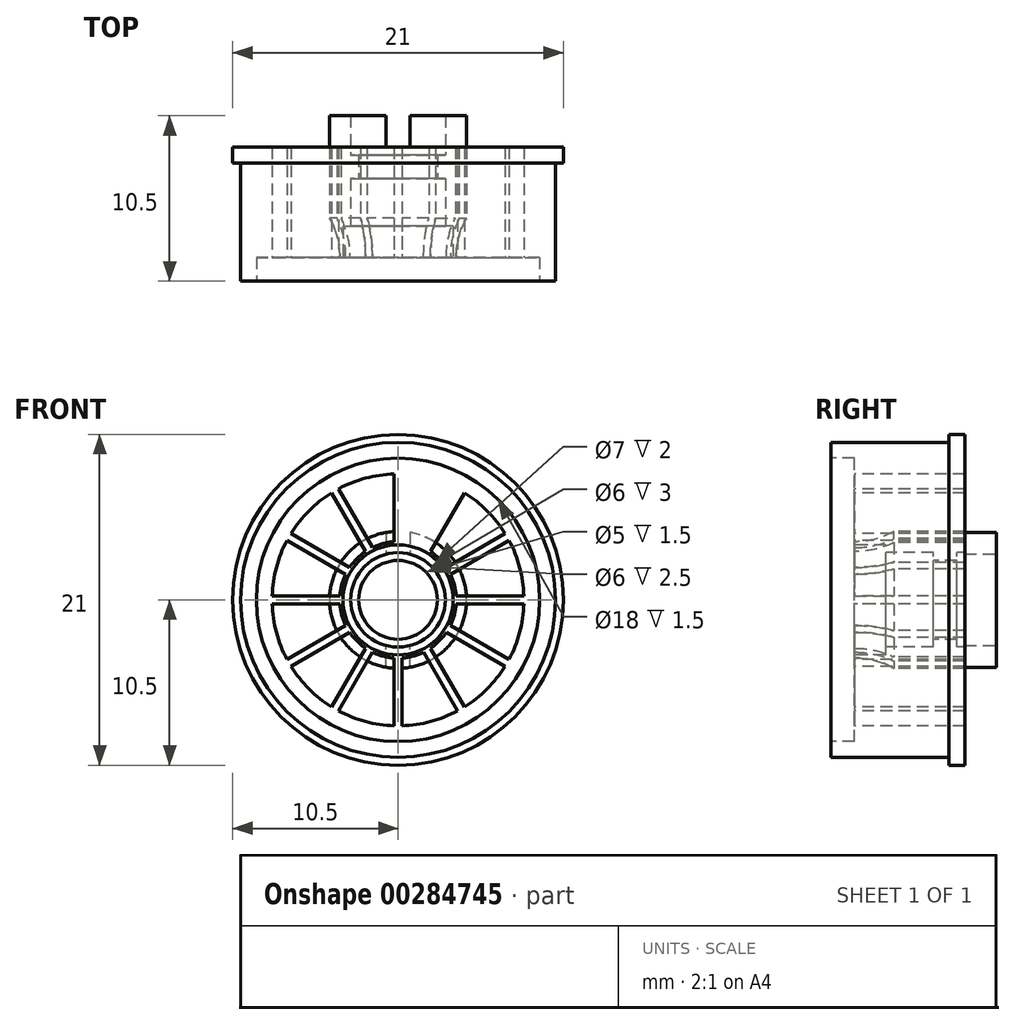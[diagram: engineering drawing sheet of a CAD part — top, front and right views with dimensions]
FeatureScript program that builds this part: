
annotation { "Feature Type Name" : "Feature", "Feature Type Description" : "" }
export const myFeature = defineFeature(function(context is Context, id is Id, definition is map)
    precondition{}
    {
        {
            var Q0;
            Q0=qCreatedBy(makeId("Front.planeOp"),FACE);
            var sketch = newSketch(context, id + "F0", { "sketchPlane" : qUnion([Q0])});
            skCircle(sketch, "E0", {"center": v(0, 0) * mm, "radius": 10.5 * mm});
            skSolve(sketch);
        }
        {
            var Q0;
            Q0=makeQuery(id+"F0.imprint","IMPRINT",FACE,{"disambiguationData":[TD([[makeQuery(id+"F0.imprint","IMPRINT",EDGE,{"derivedFrom":sQuery(id+"F0.wireOp",EDGE,"E0")}),1.0]])]});
            extrude(context, id + "F1", {"entities" : qUnion([Q0]), "depth" : 1 * mm});
        }
        {
            var Q0;
            Q0=makeQuery(id+"F1.opExtrude","CAP_FACE",FACE,{"disambiguationData":[OSD([sQuery(id+"F0.wireOp",EDGE,"E0")])],"isStart":false});
            var sketch = newSketch(context, id + "F2", { "sketchPlane" : qUnion([Q0])});
            skCircle(sketch, "E1", {"center": v(0, 0) * mm, "radius": 10 * mm});
            skSolve(sketch);
        }
        {
            var Q0;
            Q0=makeQuery(id+"F2.imprint","IMPRINT",FACE,{"disambiguationData":[TD([[makeQuery(id+"F2.imprint","IMPRINT",EDGE,{"derivedFrom":sQuery(id+"F2.wireOp",EDGE,"E1")}),1.0]])]});
            extrude(context, id + "F3", {"entities" : qUnion([Q0]), "operationType" : NewBodyOperationType.ADD, "depth" : 7.5 * mm});
        }
        {
            var Q0;
            Q0=makeQuery(id+"F3.opExtrude","CAP_FACE",FACE,{"disambiguationData":[OSD([sQuery(id+"F2.wireOp",EDGE,"E1")])],"isStart":false});
            var sketch = newSketch(context, id + "F4", { "sketchPlane" : qUnion([Q0])});
            skCircle(sketch, "E2", {"center": v(0, 0) * mm, "radius": 3.5 * mm});
            skSolve(sketch);
        }
        {
            var Q0;
            Q0=makeQuery(id+"F4.imprint","IMPRINT",FACE,{"disambiguationData":[TD([[makeQuery(id+"F4.imprint","IMPRINT",EDGE,{"derivedFrom":sQuery(id+"F4.wireOp",EDGE,"E2")}),1.0]])]});
            extrude(context, id + "F5", {"entities" : qUnion([Q0]), "operationType" : NewBodyOperationType.REMOVE, "oppositeDirection" : true, "depth" : 3.5 * mm});
        }
        {
            var Q0;
            Q0=makeQuery(id+"F5.boolean.opBoolean","COPY",FACE,{"derivedFrom":makeQuery(id+"F5.opExtrude","CAP_FACE",FACE,{"disambiguationData":[OSD([sQuery(id+"F4.wireOp",EDGE,"E2")])],"isStart":false})});
            var sketch = newSketch(context, id + "F6", { "sketchPlane" : qUnion([Q0])});
            skCircle(sketch, "E3", {"center": v(0, 0) * mm, "radius": 3 * mm});
            skSolve(sketch);
        }
        {
            var Q0;
            Q0=makeQuery(id+"F6.imprint","IMPRINT",FACE,{"disambiguationData":[TD([[makeQuery(id+"F6.imprint","IMPRINT",EDGE,{"derivedFrom":sQuery(id+"F6.wireOp",EDGE,"E3")}),1.0]])]});
            extrude(context, id + "F7", {"entities" : qUnion([Q0]), "operationType" : NewBodyOperationType.REMOVE, "oppositeDirection" : true, "depth" : 3 * mm});
        }
        {
            var Q0;
            Q0=makeQuery(id+"F7.boolean.opBoolean","COPY",FACE,{"derivedFrom":makeQuery(id+"F7.opExtrude","CAP_FACE",FACE,{"disambiguationData":[OSD([sQuery(id+"F6.wireOp",EDGE,"E3")])],"isStart":false})});
            var sketch = newSketch(context, id + "F8", { "sketchPlane" : qUnion([Q0])});
            skCircle(sketch, "E4", {"center": v(0, 0) * mm, "radius": 2.5 * mm});
            skSolve(sketch);
        }
        {
            var Q0;
            Q0=makeQuery(id+"F8.imprint","IMPRINT",FACE,{"disambiguationData":[TD([[makeQuery(id+"F8.imprint","IMPRINT",EDGE,{"derivedFrom":sQuery(id+"F8.wireOp",EDGE,"E4")}),1.0]])]});
            extrude(context, id + "F9", {"entities" : qUnion([Q0]), "operationType" : NewBodyOperationType.REMOVE, "oppositeDirection" : true, "depth" : 1.5 * mm});
        }
        {
            var Q0;
            Q0=makeQuery(id+"F9.boolean.opBoolean","COPY",FACE,{"derivedFrom":makeQuery(id+"F9.opExtrude","CAP_FACE",FACE,{"disambiguationData":[OSD([sQuery(id+"F8.wireOp",EDGE,"E4")])],"isStart":false})});
            var sketch = newSketch(context, id + "F10", { "sketchPlane" : qUnion([Q0])});
            skCircle(sketch, "E5", {"center": v(0, 0) * mm, "radius": 3 * mm});
            skSolve(sketch);
        }
        {
            var Q0;
            Q0=qSketchRegion(id+"F10",true);
            extrude(context, id + "F11", {"entities" : qUnion([Q0]), "operationType" : NewBodyOperationType.REMOVE, "oppositeDirection" : true, "depth" : 25 * mm});
        }
        {
            var Q0;
            Q0=makeQuery(id+"F3.opExtrude","CAP_FACE",FACE,{"disambiguationData":[OSD([sQuery(id+"F2.wireOp",EDGE,"E1")])],"isStart":false});
            var sketch = newSketch(context, id + "F12", { "sketchPlane" : qUnion([Q0])});
            skCircle(sketch, "E6", {"center": v(0, 0) * mm, "radius": 9 * mm});
            skSolve(sketch);
        }
        {
            var Q0;
            Q0=makeQuery(id+"F1.opExtrude","CAP_FACE",FACE,{"disambiguationData":[OSD([sQuery(id+"F0.wireOp",EDGE,"E0")])],"isStart":true});
            var sketch = newSketch(context, id + "F13", { "sketchPlane" : qUnion([Q0])});
            skCircle(sketch, "E7", {"center": v(0, 0) * mm, "radius": 9 * mm});
            skCircle(sketch, "E8", {"center": v(0, 0) * mm, "radius": 4.35 * mm});
            skSolve(sketch);
        }
        {
            var Q0;
            Q0=makeQuery(id+"F13.imprint","IMPRINT",FACE,{"disambiguationData":[TD([[makeQuery(id+"F13.imprint","IMPRINT",EDGE,{"derivedFrom":sQuery(id+"F13.wireOp",EDGE,"E7")}),1.0]])]});
            extrude(context, id + "F14", {"entities" : qUnion([Q0]), "operationType" : NewBodyOperationType.REMOVE, "oppositeDirection" : true, "depth" : 4.5 * mm});
        }
        {
            var Q0;
            Q0=makeQuery(id+"F12.imprint","IMPRINT",FACE,{"disambiguationData":[TD([[makeQuery(id+"F12.imprint","IMPRINT",EDGE,{"derivedFrom":sQuery(id+"F12.wireOp",EDGE,"E6")}),1.0]])]});
            extrude(context, id + "F15", {"entities" : qUnion([Q0]), "operationType" : NewBodyOperationType.REMOVE, "oppositeDirection" : true, "depth" : 1.5 * mm});
        }
        {
            var Q0;
            Q0=makeQuery(id+"F15.boolean.opBoolean","COPY",FACE,{"derivedFrom":makeQuery(id+"F15.opExtrude","CAP_FACE",FACE,{"disambiguationData":[OSD([sQuery(id+"F4.wireOp",EDGE,"E2"),sQuery(id+"F12.wireOp",EDGE,"E6")])],"isStart":false})});
            var sketch = newSketch(context, id + "F16", { "sketchPlane" : qUnion([Q0])});
            skCircle(sketch, "E9.0", {"center": v(0, 0) * mm, "radius": 8 * mm});
            skCircle(sketch, "E10.0", {"center": v(0, 0) * mm, "radius": 3.7 * mm});
            skLineSegment(sketch, "E11", {"start": v(-1.85, 3.2) * mm, "end": v(-4, 6.93) * mm});
            skLineSegment(sketch, "E12", {"start": v(0, 3.7) * mm, "end": v(0, 8) * mm});
            skLineSegment(sketch, "E13", {"start": v(-0.25, 3.7) * mm, "end": v(-0.25, 8) * mm});
            skLineSegment(sketch, "E14.0.MirrorCS", {"start": v(0.25, 3.7) * mm, "end": v(0.25, 8) * mm});
            skLineSegment(sketch, "E15", {"start": v(-2.06, 3.07) * mm, "end": v(-4.21, 6.8) * mm});
            skLineSegment(sketch, "E16.0.MirrorCS", {"start": v(-1.63, 3.32) * mm, "end": v(-3.78, 7.05) * mm});
            skLineSegment(sketch, "E17.1.0", {"start": v(-3.07, 2.06) * mm, "end": v(-6.8, 4.21) * mm});
            skLineSegment(sketch, "E17.2.0", {"start": v(-3.7, 0.25) * mm, "end": v(-8, 0.25) * mm});
            skLineSegment(sketch, "E17.2.1", {"start": v(-3.32, 1.63) * mm, "end": v(-7.05, 3.78) * mm});
            skLineSegment(sketch, "E17.3.0", {"start": v(-3.32, -1.63) * mm, "end": v(-7.05, -3.78) * mm});
            skLineSegment(sketch, "E17.3.1", {"start": v(-3.7, -0.25) * mm, "end": v(-8, -0.25) * mm});
            skLineSegment(sketch, "E17.4.0", {"start": v(-2.06, -3.07) * mm, "end": v(-4.21, -6.8) * mm});
            skLineSegment(sketch, "E17.4.1", {"start": v(-3.07, -2.06) * mm, "end": v(-6.8, -4.21) * mm});
            skLineSegment(sketch, "E17.5.0", {"start": v(-0.25, -3.7) * mm, "end": v(-0.25, -8) * mm});
            skLineSegment(sketch, "E17.5.1", {"start": v(-1.63, -3.32) * mm, "end": v(-3.78, -7.05) * mm});
            skLineSegment(sketch, "E17.6.0", {"start": v(1.63, -3.32) * mm, "end": v(3.78, -7.05) * mm});
            skLineSegment(sketch, "E17.6.1", {"start": v(0.25, -3.7) * mm, "end": v(0.25, -8) * mm});
            skLineSegment(sketch, "E17.7.0", {"start": v(3.07, -2.06) * mm, "end": v(6.8, -4.21) * mm});
            skLineSegment(sketch, "E17.7.1", {"start": v(2.06, -3.07) * mm, "end": v(4.21, -6.8) * mm});
            skLineSegment(sketch, "E17.8.0", {"start": v(3.7, -0.25) * mm, "end": v(8, -0.25) * mm});
            skLineSegment(sketch, "E17.8.1", {"start": v(3.32, -1.63) * mm, "end": v(7.05, -3.78) * mm});
            skLineSegment(sketch, "E17.9.0", {"start": v(3.32, 1.63) * mm, "end": v(7.05, 3.78) * mm});
            skLineSegment(sketch, "E17.9.1", {"start": v(3.7, 0.25) * mm, "end": v(8, 0.25) * mm});
            skLineSegment(sketch, "E17.10.0", {"start": v(2.06, 3.07) * mm, "end": v(4.21, 6.8) * mm});
            skLineSegment(sketch, "E17.10.1", {"start": v(3.07, 2.06) * mm, "end": v(6.8, 4.21) * mm});
            skLineSegment(sketch, "E17.11.1", {"start": v(1.63, 3.32) * mm, "end": v(3.78, 7.05) * mm});
            skSolve(sketch);
        }
        {
            var Q0;
            {var subQ1=sQuery(id+"F16.wireOp",EDGE,"E13");Q0=makeQuery(id+"F16.imprint","IMPRINT",FACE,{"disambiguationData":[TD([[makeQuery(id+"F16.imprint","IMPRINT",EDGE,{"derivedFrom":subQ1}),1.0]])]});}
            var Q1;
            {var subQ1=sQuery(id+"F16.wireOp",EDGE,"E14.0.MirrorCS");Q1=makeQuery(id+"F16.imprint","IMPRINT",FACE,{"disambiguationData":[TD([[makeQuery(id+"F16.imprint","IMPRINT",EDGE,{"derivedFrom":subQ1}),-1.0]])]});}
            var Q2;
            {var subQ1=sQuery(id+"F16.wireOp",EDGE,"E17.10.0");Q2=makeQuery(id+"F16.imprint","IMPRINT",FACE,{"disambiguationData":[TD([[makeQuery(id+"F16.imprint","IMPRINT",EDGE,{"derivedFrom":subQ1}),-1.0]])]});}
            var Q3;
            {var subQ1=sQuery(id+"F16.wireOp",EDGE,"E17.9.0");Q3=makeQuery(id+"F16.imprint","IMPRINT",FACE,{"disambiguationData":[TD([[makeQuery(id+"F16.imprint","IMPRINT",EDGE,{"derivedFrom":subQ1}),-1.0]])]});}
            var Q4;
            {var subQ1=sQuery(id+"F16.wireOp",EDGE,"E17.8.0");Q4=makeQuery(id+"F16.imprint","IMPRINT",FACE,{"disambiguationData":[TD([[makeQuery(id+"F16.imprint","IMPRINT",EDGE,{"derivedFrom":subQ1}),-1.0]])]});}
            var Q5;
            {var subQ1=sQuery(id+"F16.wireOp",EDGE,"E17.7.0");Q5=makeQuery(id+"F16.imprint","IMPRINT",FACE,{"disambiguationData":[TD([[makeQuery(id+"F16.imprint","IMPRINT",EDGE,{"derivedFrom":subQ1}),-1.0]])]});}
            var Q6;
            {var subQ2=sQuery(id+"F16.wireOp",EDGE,"E17.1.0");Q6=makeQuery(id+"F16.imprint","IMPRINT",FACE,{"disambiguationData":[TD([[makeQuery(id+"F16.imprint","IMPRINT",EDGE,{"derivedFrom":subQ2}),-1.0]])]});}
            var Q7;
            {var subQ2=sQuery(id+"F16.wireOp",EDGE,"E17.2.0");Q7=makeQuery(id+"F16.imprint","IMPRINT",FACE,{"disambiguationData":[TD([[makeQuery(id+"F16.imprint","IMPRINT",EDGE,{"derivedFrom":subQ2}),-1.0]])]});}
            var Q8;
            {var subQ2=sQuery(id+"F16.wireOp",EDGE,"E17.3.0");Q8=makeQuery(id+"F16.imprint","IMPRINT",FACE,{"disambiguationData":[TD([[makeQuery(id+"F16.imprint","IMPRINT",EDGE,{"derivedFrom":subQ2}),-1.0]])]});}
            var Q9;
            {var subQ1=sQuery(id+"F16.wireOp",EDGE,"E17.4.0");Q9=makeQuery(id+"F16.imprint","IMPRINT",FACE,{"disambiguationData":[TD([[makeQuery(id+"F16.imprint","IMPRINT",EDGE,{"derivedFrom":subQ1}),-1.0]])]});}
            var Q10;
            {var subQ1=sQuery(id+"F16.wireOp",EDGE,"E17.5.0");Q10=makeQuery(id+"F16.imprint","IMPRINT",FACE,{"disambiguationData":[TD([[makeQuery(id+"F16.imprint","IMPRINT",EDGE,{"derivedFrom":subQ1}),-1.0]])]});}
            var Q11;
            {var subQ1=sQuery(id+"F16.wireOp",EDGE,"E17.6.0");Q11=makeQuery(id+"F16.imprint","IMPRINT",FACE,{"disambiguationData":[TD([[makeQuery(id+"F16.imprint","IMPRINT",EDGE,{"derivedFrom":subQ1}),-1.0]])]});}
            extrude(context, id + "F17", {"entities" : qUnion([Q0, Q1, Q2, Q3, Q4, Q5, Q6, Q7, Q8, Q9, Q10, Q11]), "operationType" : NewBodyOperationType.REMOVE, "oppositeDirection" : true, "depth" : 2.5 * mm});
        }
        {
            var Q0;
            {var subQ0=sQuery(id+"F16.wireOp",EDGE,"E10.0");Q0=makeQuery(id+"F17.boolean.opBoolean","COPY",EDGE,{"derivedFrom":makeQuery(id+"F17.opExtrude","CAP_EDGE",EDGE,{"disambiguationData":[OSD([subQ0]),TDD([makeQuery(id+"F16.imprint","IMPRINT",EDGE,{"disambiguationData":[TD([[makeQuery(id+"F16.imprint","INTERSECT",VERTEX,{"derivedFrom":[subQ0,sQuery(id+"F16.wireOp",EDGE,"E17.1.0")]}),1.0]])],"derivedFrom":subQ0})])],"isStart":false})});}
            var Q1;
            {var subQ0=sQuery(id+"F16.wireOp",EDGE,"E10.0");Q1=makeQuery(id+"F17.boolean.opBoolean","COPY",EDGE,{"derivedFrom":makeQuery(id+"F17.opExtrude","CAP_EDGE",EDGE,{"disambiguationData":[OSD([subQ0]),TDD([makeQuery(id+"F16.imprint","IMPRINT",EDGE,{"disambiguationData":[TD([[makeQuery(id+"F16.imprint","INTERSECT",VERTEX,{"derivedFrom":[subQ0,sQuery(id+"F16.wireOp",EDGE,"E13")]}),-1.0]])],"derivedFrom":subQ0})])],"isStart":false})});}
            var Q2;
            {var subQ0=sQuery(id+"F16.wireOp",EDGE,"E10.0");Q2=makeQuery(id+"F17.boolean.opBoolean","COPY",EDGE,{"derivedFrom":makeQuery(id+"F17.opExtrude","CAP_EDGE",EDGE,{"disambiguationData":[OSD([subQ0]),TDD([makeQuery(id+"F16.imprint","IMPRINT",EDGE,{"disambiguationData":[TD([[makeQuery(id+"F16.imprint","INTERSECT",VERTEX,{"derivedFrom":[subQ0,sQuery(id+"F16.wireOp",EDGE,"E14.0.MirrorCS")]}),1.0]])],"derivedFrom":subQ0})])],"isStart":false})});}
            var Q3;
            {var subQ0=sQuery(id+"F16.wireOp",EDGE,"E10.0");Q3=makeQuery(id+"F17.boolean.opBoolean","COPY",EDGE,{"derivedFrom":makeQuery(id+"F17.opExtrude","CAP_EDGE",EDGE,{"disambiguationData":[OSD([subQ0]),TDD([makeQuery(id+"F16.imprint","IMPRINT",EDGE,{"disambiguationData":[TD([[makeQuery(id+"F16.imprint","INTERSECT",VERTEX,{"derivedFrom":[subQ0,sQuery(id+"F16.wireOp",EDGE,"E17.10.0")]}),1.0]])],"derivedFrom":subQ0})])],"isStart":false})});}
            var Q4;
            {var subQ0=sQuery(id+"F16.wireOp",EDGE,"E10.0");Q4=makeQuery(id+"F17.boolean.opBoolean","COPY",EDGE,{"derivedFrom":makeQuery(id+"F17.opExtrude","CAP_EDGE",EDGE,{"disambiguationData":[OSD([subQ0]),TDD([makeQuery(id+"F16.imprint","IMPRINT",EDGE,{"disambiguationData":[TD([[makeQuery(id+"F16.imprint","INTERSECT",VERTEX,{"derivedFrom":[subQ0,sQuery(id+"F16.wireOp",EDGE,"E17.2.0")]}),1.0]])],"derivedFrom":subQ0})])],"isStart":false})});}
            var Q5;
            {var subQ0=sQuery(id+"F16.wireOp",EDGE,"E10.0");Q5=makeQuery(id+"F17.boolean.opBoolean","COPY",EDGE,{"derivedFrom":makeQuery(id+"F17.opExtrude","CAP_EDGE",EDGE,{"disambiguationData":[OSD([subQ0]),TDD([makeQuery(id+"F16.imprint","IMPRINT",EDGE,{"disambiguationData":[TD([[makeQuery(id+"F16.imprint","INTERSECT",VERTEX,{"derivedFrom":[subQ0,sQuery(id+"F16.wireOp",EDGE,"E17.3.0")]}),1.0]])],"derivedFrom":subQ0})])],"isStart":false})});}
            var Q6;
            {var subQ0=sQuery(id+"F16.wireOp",EDGE,"E10.0");Q6=makeQuery(id+"F17.boolean.opBoolean","COPY",EDGE,{"derivedFrom":makeQuery(id+"F17.opExtrude","CAP_EDGE",EDGE,{"disambiguationData":[OSD([subQ0]),TDD([makeQuery(id+"F16.imprint","IMPRINT",EDGE,{"disambiguationData":[TD([[makeQuery(id+"F16.imprint","INTERSECT",VERTEX,{"derivedFrom":[subQ0,sQuery(id+"F16.wireOp",EDGE,"E17.9.0")]}),1.0]])],"derivedFrom":subQ0})])],"isStart":false})});}
            var Q7;
            {var subQ0=sQuery(id+"F16.wireOp",EDGE,"E10.0");Q7=makeQuery(id+"F17.boolean.opBoolean","COPY",EDGE,{"derivedFrom":makeQuery(id+"F17.opExtrude","CAP_EDGE",EDGE,{"disambiguationData":[OSD([subQ0]),TDD([makeQuery(id+"F16.imprint","IMPRINT",EDGE,{"disambiguationData":[TD([[makeQuery(id+"F16.imprint","INTERSECT",VERTEX,{"derivedFrom":[subQ0,sQuery(id+"F16.wireOp",EDGE,"E17.8.0")]}),1.0]])],"derivedFrom":subQ0})])],"isStart":false})});}
            var Q8;
            {var subQ0=sQuery(id+"F16.wireOp",EDGE,"E10.0");Q8=makeQuery(id+"F17.boolean.opBoolean","COPY",EDGE,{"derivedFrom":makeQuery(id+"F17.opExtrude","CAP_EDGE",EDGE,{"disambiguationData":[OSD([subQ0]),TDD([makeQuery(id+"F16.imprint","IMPRINT",EDGE,{"disambiguationData":[TD([[makeQuery(id+"F16.imprint","INTERSECT",VERTEX,{"derivedFrom":[subQ0,sQuery(id+"F16.wireOp",EDGE,"E17.7.0")]}),1.0]])],"derivedFrom":subQ0})])],"isStart":false})});}
            var Q9;
            {var subQ0=sQuery(id+"F16.wireOp",EDGE,"E10.0");Q9=makeQuery(id+"F17.boolean.opBoolean","COPY",EDGE,{"derivedFrom":makeQuery(id+"F17.opExtrude","CAP_EDGE",EDGE,{"disambiguationData":[OSD([subQ0]),TDD([makeQuery(id+"F16.imprint","IMPRINT",EDGE,{"disambiguationData":[TD([[makeQuery(id+"F16.imprint","INTERSECT",VERTEX,{"derivedFrom":[subQ0,sQuery(id+"F16.wireOp",EDGE,"E17.6.0")]}),1.0]])],"derivedFrom":subQ0})])],"isStart":false})});}
            var Q10;
            {var subQ0=sQuery(id+"F16.wireOp",EDGE,"E10.0");Q10=makeQuery(id+"F17.boolean.opBoolean","COPY",EDGE,{"derivedFrom":makeQuery(id+"F17.opExtrude","CAP_EDGE",EDGE,{"disambiguationData":[OSD([subQ0]),TDD([makeQuery(id+"F16.imprint","IMPRINT",EDGE,{"disambiguationData":[TD([[makeQuery(id+"F16.imprint","INTERSECT",VERTEX,{"derivedFrom":[subQ0,sQuery(id+"F16.wireOp",EDGE,"E17.5.0")]}),1.0]])],"derivedFrom":subQ0})])],"isStart":false})});}
            var Q11;
            {var subQ0=sQuery(id+"F16.wireOp",EDGE,"E10.0");Q11=makeQuery(id+"F17.boolean.opBoolean","COPY",EDGE,{"derivedFrom":makeQuery(id+"F17.opExtrude","CAP_EDGE",EDGE,{"disambiguationData":[OSD([subQ0]),TDD([makeQuery(id+"F16.imprint","IMPRINT",EDGE,{"disambiguationData":[TD([[makeQuery(id+"F16.imprint","INTERSECT",VERTEX,{"derivedFrom":[subQ0,sQuery(id+"F16.wireOp",EDGE,"E17.4.0")]}),1.0]])],"derivedFrom":subQ0})])],"isStart":false})});}
            fillet(context, id + "F18", {"entities" : qUnion([Q0, Q1, Q2, Q3, Q4, Q5, Q6, Q7, Q8, Q9, Q10, Q11]), "radius" : 5 * mm, "tangentPropagation" : true, "allowEdgeOverflow" : false});
        }
        {
            var Q0;
            Q0=makeQuery(id+"F14.boolean.opBoolean","SPLIT",FACE,{"disambiguationData":[TD([makeQuery(id+"F11.boolean.opBoolean","COPY",FACE,{"derivedFrom":makeQuery(id+"F11.opExtrude","SWEPT_FACE",FACE,{"disambiguationData":[OSD([sQuery(id+"F10.wireOp",EDGE,"E5")])]})})])],"derivedFrom":makeQuery(id+"F1.opExtrude","CAP_FACE",FACE,{"disambiguationData":[OSD([sQuery(id+"F0.wireOp",EDGE,"E0")])],"isStart":true})});
            extrude(context, id + "F19", {"entities" : qUnion([Q0]), "operationType" : NewBodyOperationType.ADD, "depth" : 2 * mm});
        }
        {
            var Q0;
            Q0=makeQuery(id+"F19.opExtrude","CAP_FACE",FACE,{"disambiguationData":[OSD([sQuery(id+"F0.wireOp",EDGE,"E0")])],"isStart":false});
            var sketch = newSketch(context, id + "F20", { "sketchPlane" : qUnion([Q0])});
            skLineSegment(sketch, "E18", {"start": v(0, 3) * mm, "end": v(0, 4.35) * mm});
            skLineSegment(sketch, "E19", {"start": v(-0.75, 4.28) * mm, "end": v(-0.75, 2.9) * mm});
            skLineSegment(sketch, "E20.0.MirrorCS", {"start": v(0.75, 4.28) * mm, "end": v(0.75, 2.9) * mm});
            skLineSegment(sketch, "E21", {"start": v(0, 0) * mm, "end": v(2.07, 0) * mm});
            skLineSegment(sketch, "E22.0.MirrorCS", {"start": v(-0.75, -4.28) * mm, "end": v(-0.75, -2.9) * mm});
            skLineSegment(sketch, "E23.0.MirrorCS", {"start": v(0.75, -4.28) * mm, "end": v(0.75, -2.9) * mm});
            skSolve(sketch);
        }
        {
            var Q0;
            {var subQ2=sQuery(id+"F20.wireOp",EDGE,"E18");Q0=makeQuery(id+"F20.imprint","IMPRINT",FACE,{"disambiguationData":[TD([[makeQuery(id+"F20.imprint","IMPRINT",EDGE,{"derivedFrom":subQ2}),1.0]])]});}
            var Q1;
            {var subQ2=sQuery(id+"F20.wireOp",EDGE,"E18");Q1=makeQuery(id+"F20.imprint","IMPRINT",FACE,{"disambiguationData":[TD([[makeQuery(id+"F20.imprint","IMPRINT",EDGE,{"derivedFrom":subQ2}),-1.0]])]});}
            var Q2;
            {var subQ2=sQuery(id+"F20.wireOp",EDGE,"E22.0.MirrorCS");Q2=makeQuery(id+"F20.imprint","IMPRINT",FACE,{"disambiguationData":[TD([[makeQuery(id+"F20.imprint","IMPRINT",EDGE,{"derivedFrom":subQ2}),-1.0]])]});}
            extrude(context, id + "F21", {"entities" : qUnion([Q0, Q1, Q2]), "operationType" : NewBodyOperationType.REMOVE, "oppositeDirection" : true, "depth" : 2 * mm});
        }
        {
            var Q0;
            Q0=makeQuery(id+"F14.boolean.opBoolean","COPY",FACE,{"derivedFrom":makeQuery(id+"F14.opExtrude","CAP_FACE",FACE,{"disambiguationData":[OSD([sQuery(id+"F13.wireOp",EDGE,"E7"),sQuery(id+"F13.wireOp",EDGE,"E8")])],"isStart":false})});
            var Q1;
            {var subQ0=sQuery(id+"F0.wireOp",EDGE,"E0");Q1=makeQuery(id+"F14.boolean.opBoolean","SPLIT",FACE,{"disambiguationData":[TD([makeQuery(id+"F1.opExtrude","SWEPT_FACE",FACE,{"disambiguationData":[OSD([subQ0])]})])],"derivedFrom":makeQuery(id+"F1.opExtrude","CAP_FACE",FACE,{"disambiguationData":[OSD([subQ0])],"isStart":true})});}
            extrude(context, id + "F22", {"entities" : qUnion([Q0]), "operationType" : NewBodyOperationType.ADD, "endBound" : BoundingType.UP_TO_SURFACE, "endBoundEntityFace" : qUnion([Q1]), "depth" : 25 * mm});
        }
    });
